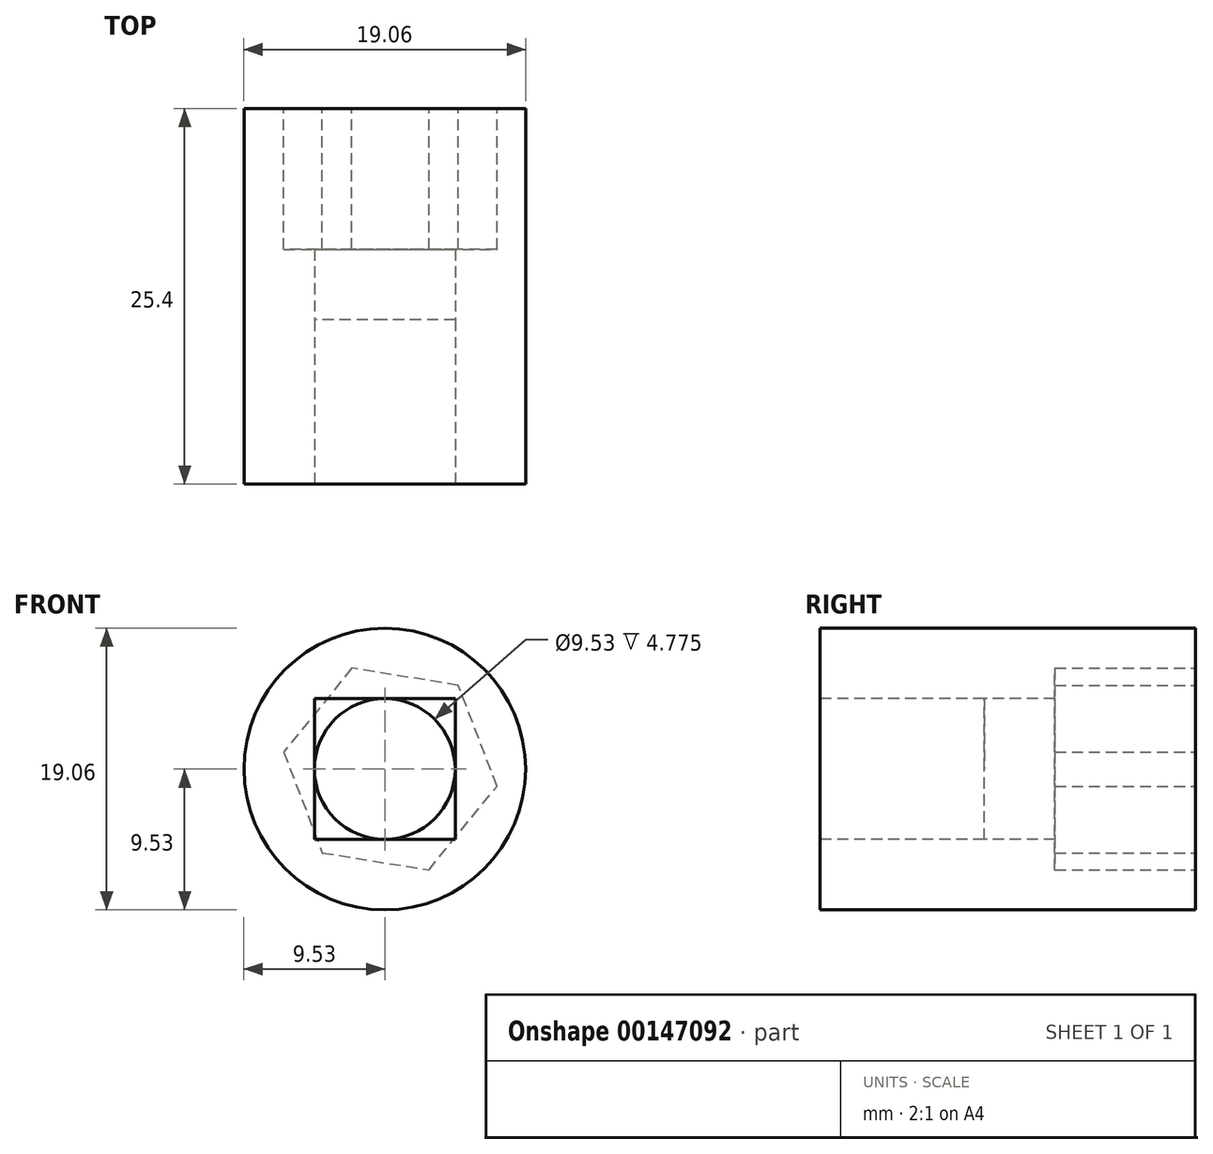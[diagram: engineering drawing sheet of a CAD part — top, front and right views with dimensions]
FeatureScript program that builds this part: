
annotation { "Feature Type Name" : "Feature", "Feature Type Description" : "" }
export const myFeature = defineFeature(function(context is Context, id is Id, definition is map)
    precondition{}
    {
        {
            var Q0;
            Q0=qCreatedBy(makeId("Front.planeOp"),FACE);
            var sketch = newSketch(context, id + "F0", { "sketchPlane" : qUnion([Q0])});
            skCircle(sketch, "E0", {"center": v(0, 0) * mm, "radius": 9.53 * mm});
            skSolve(sketch);
        }
        {
            var Q0;
            Q0 = qSketchRegion(id + "F0", true);
            extrude(context, id + "F1", {"entities" : qUnion([Q0]), "oppositeDirection" : true, "depth" : 25.4 * mm});
        }
        {
            var Q0;
            Q0=qCreatedBy(makeId("Front.planeOp"),FACE);
            var sketch = newSketch(context, id + "F2", { "sketchPlane" : qUnion([Q0])});
            skLineSegment(sketch, "E1.bottom", {"start": v(4.76, -4.76) * mm, "end": v(-4.76, -4.76) * mm});
            skLineSegment(sketch, "E1.top", {"start": v(4.76, 4.76) * mm, "end": v(-4.76, 4.76) * mm});
            skLineSegment(sketch, "E1.left", {"start": v(4.76, -4.76) * mm, "end": v(4.76, 4.76) * mm});
            skLineSegment(sketch, "E1.right", {"start": v(-4.76, -4.76) * mm, "end": v(-4.76, 4.76) * mm});
            skPoint(sketch, "E1.middle", {"position": v(0, 0) * mm});
            skCircle(sketch, "E2", {"center": v(0, 0) * mm, "radius": 4.76 * mm});
            skSolve(sketch);
        }
        {
            var Q0;
            {var subQ0=sQuery(id+"F2.wireOp",EDGE,"E2");var subQ1=makeQuery(id+"F2.imprint","INTERSECT",VERTEX,{"derivedFrom":[sQuery(id+"F2.wireOp",EDGE,"E1.top"),subQ0]});Q0=makeQuery(id+"F2.imprint","IMPRINT",FACE,{"disambiguationData":[TD([[makeQuery(id+"F2.imprint","IMPRINT",EDGE,{"disambiguationData":[TD([[subQ1,1.0]])],"derivedFrom":subQ0}),1.0]])]});}
            extrude(context, id + "F3", {"entities" : qUnion([Q0]), "operationType" : NewBodyOperationType.REMOVE, "endBound" : BoundingType.THROUGH_ALL, "oppositeDirection" : true, "depth" : 25.4 * mm});
        }
        {
            var Q0;
            Q0 = qSketchRegion(id + "F2", true);
            extrude(context, id + "F4", {"entities" : qUnion([Q0]), "operationType" : NewBodyOperationType.REMOVE, "oppositeDirection" : true, "depth" : 11.1 * mm});
        }
        {
            var Q0;
            Q0=makeQuery(id+"F1.opExtrude","CAP_FACE",FACE,{"disambiguationData":[OSD([sQuery(id+"F0.wireOp",EDGE,"E0")])],"isStart":false});
            var sketch = newSketch(context, id + "F5", { "sketchPlane" : qUnion([Q0])});
            skCircle(sketch, "E3.cCircle", {"center": v(-0.38, 0) * mm, "radius": 6.32 * mm, "construction": true});
            skLineSegment(sketch, "E3.0", {"start": v(6.83, 1.15) * mm, "end": v(4.23, -5.67) * mm});
            skLineSegment(sketch, "E3.1", {"start": v(4.23, -5.67) * mm, "end": v(-2.99, -6.82) * mm});
            skLineSegment(sketch, "E3.2", {"start": v(-2.99, -6.82) * mm, "end": v(-7.59, -1.15) * mm});
            skLineSegment(sketch, "E3.3", {"start": v(-7.59, -1.15) * mm, "end": v(-4.98, 5.67) * mm});
            skLineSegment(sketch, "E3.4", {"start": v(-4.98, 5.67) * mm, "end": v(2.23, 6.82) * mm});
            skLineSegment(sketch, "E3.5", {"start": v(2.23, 6.82) * mm, "end": v(6.83, 1.15) * mm});
            skPoint(sketch, "E3.0.midPoint", {"position": v(5.53, -2.26) * mm});
            skSolve(sketch);
        }
        {
            var Q0;
            Q0 = qSketchRegion(id + "F5", true);
            extrude(context, id + "F6", {"entities" : qUnion([Q0]), "operationType" : NewBodyOperationType.REMOVE, "oppositeDirection" : true, "depth" : 9.52 * mm});
        }
    });
